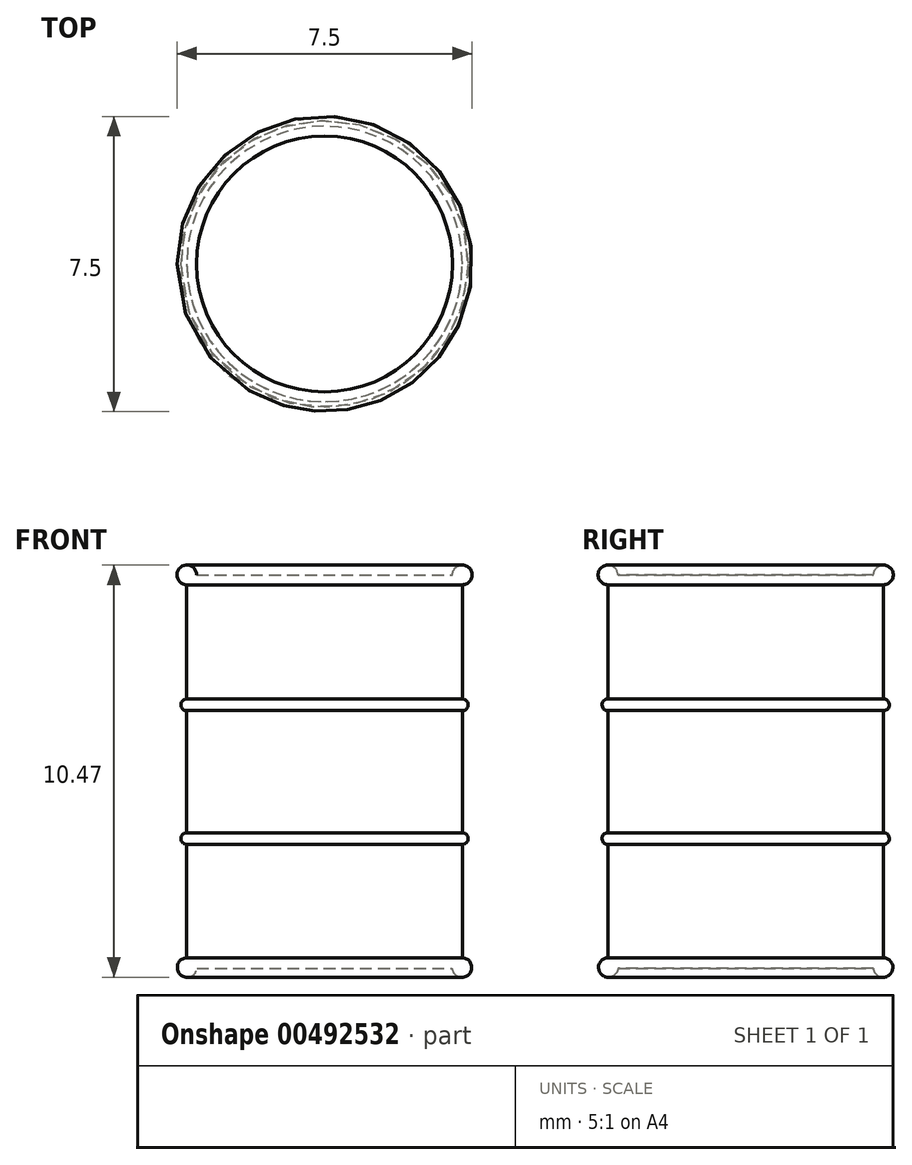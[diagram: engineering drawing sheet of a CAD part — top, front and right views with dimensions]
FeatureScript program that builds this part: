
annotation { "Feature Type Name" : "Feature", "Feature Type Description" : "" }
export const myFeature = defineFeature(function(context is Context, id is Id, definition is map)
    precondition{}
    {
        {
            var Q0;
            Q0=qCreatedBy(makeId("Top.planeOp"),FACE);
            var sketch = newSketch(context, id + "F0", { "sketchPlane" : qUnion([Q0])});
            skCircle(sketch, "E0", {"center": v(0, 0) * mm, "radius": 3.5 * mm});
            skCircle(sketch, "E1", {"center": v(-0.76, -16.93) * mm, "radius": 0.77 * mm});
            skSolve(sketch);
        }
        {
            var Q0;
            Q0=makeQuery(id+"F0.imprint","IMPRINT",FACE,{"disambiguationData":[TD([[makeQuery(id+"F0.imprint","IMPRINT",EDGE,{"derivedFrom":sQuery(id+"F0.wireOp",EDGE,"E0")}),1.0]])]});
            extrude(context, id + "F1", {"entities" : qUnion([Q0]), "oppositeDirection" : true, "depth" : 10 * mm});
        }
        {
            var Q0;
            Q0=qCreatedBy(makeId("Front.planeOp"),FACE);
            var sketch = newSketch(context, id + "F2", { "sketchPlane" : qUnion([Q0])});
            skCircle(sketch, "E2", {"center": v(-3.5, 0) * mm, "radius": 0.25 * mm});
            skCircle(sketch, "E3", {"center": v(-3.5, -9.98) * mm, "radius": 0.25 * mm});
            skCircle(sketch, "E4", {"center": v(-3.5, -3.3) * mm, "radius": 0.15 * mm});
            skCircle(sketch, "E5", {"center": v(-3.5, -6.7) * mm, "radius": 0.15 * mm});
            skSolve(sketch);
        }
        {
            var Q0;
            Q0 = qSketchRegion(id + "F2", true);
            var Q1;
            Q1=makeQuery(id+"F1.opExtrude","SWEPT_FACE",FACE,{"disambiguationData":[OSD([sQuery(id+"F0.wireOp",EDGE,"E0")])]});
            revolve(context, id + "F3", {"operationType" : NewBodyOperationType.ADD, "surfaceOperationType" : NewSurfaceOperationType.NEW, "entities" : qUnion([Q0]), "axis" : qUnion([Q1]), "revolveType" : RevolveType.FULL});
        }
    });
